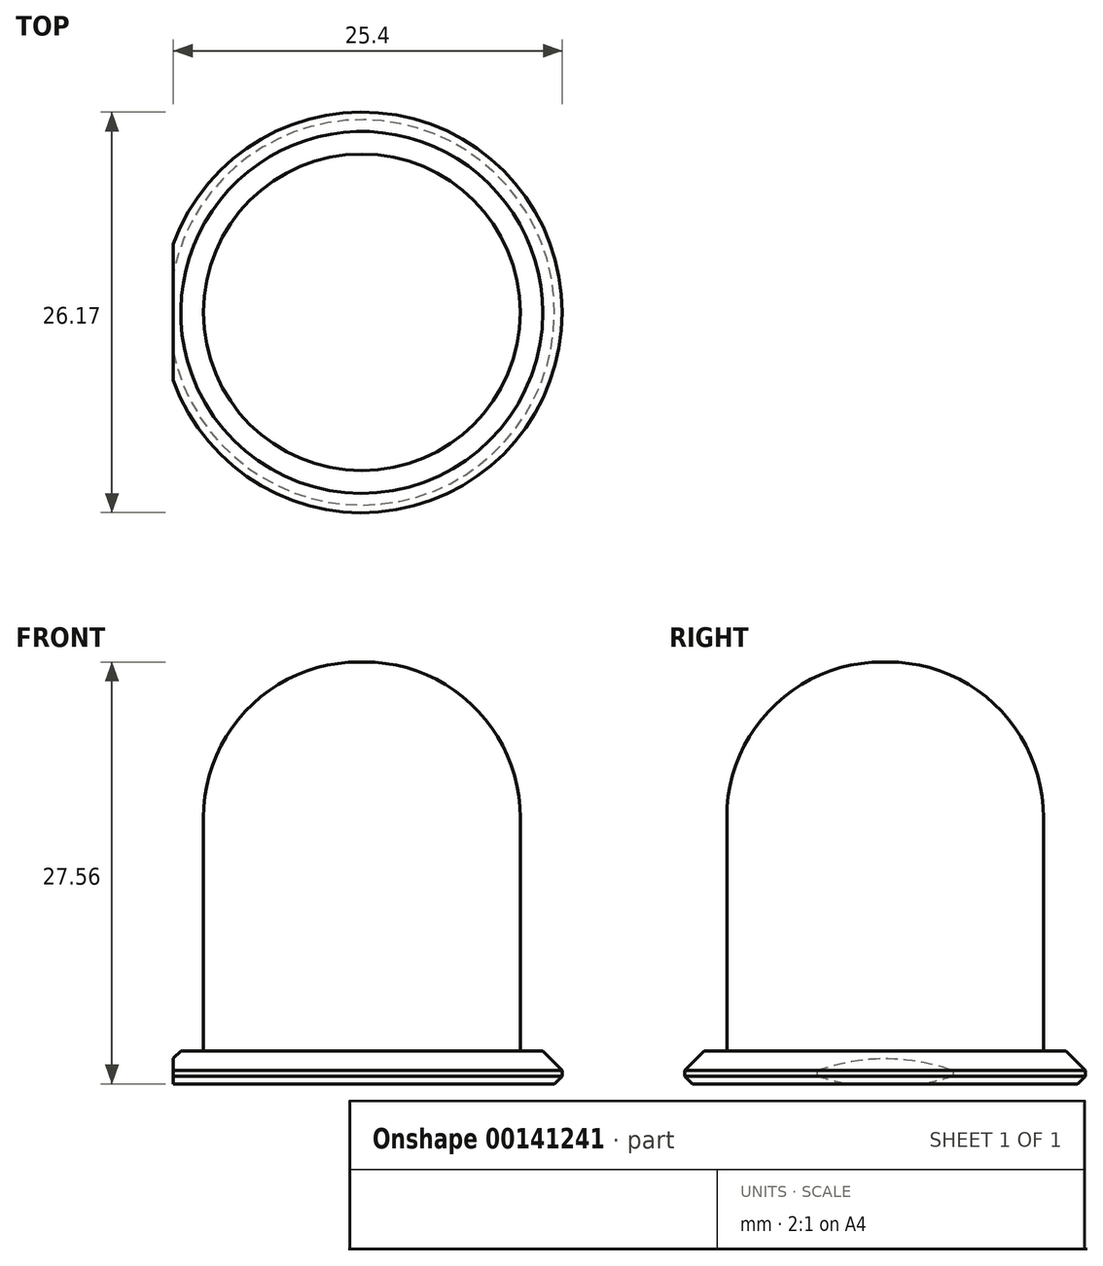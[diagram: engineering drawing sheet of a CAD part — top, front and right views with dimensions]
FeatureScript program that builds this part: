
annotation { "Feature Type Name" : "Feature", "Feature Type Description" : "" }
export const myFeature = defineFeature(function(context is Context, id is Id, definition is map)
    precondition{}
    {
        {
            var Q0;
            Q0=qCreatedBy(makeId("Top.planeOp"),FACE);
            var sketch = newSketch(context, id + "F0", { "sketchPlane" : qUnion([Q0])});
            skLineSegment(sketch, "E0", {"start": v(-68, 8.9) * mm, "end": v(-68, 0) * mm});
            skArc(sketch, "E1", {"start": v(-68, 0) * mm, "mid": v(-42.6, 4.44) * mm, "end": v(-68, 8.9) * mm});
            skSolve(sketch);
        }
        {
            var Q0;
            Q0=makeQuery(id+"F0.imprint","IMPRINT",FACE,{"disambiguationData":[TD([[makeQuery(id+"F0.imprint","IMPRINT",EDGE,{"derivedFrom":sQuery(id+"F0.wireOp",EDGE,"E0")}),1.0]])]});
            extrude(context, id + "F1", {"entities" : qUnion([Q0]), "depth" : 2.16 * mm});
        }
        {
            var Q0;
            Q0=makeQuery(id+"F1.opExtrude","CAP_FACE",FACE,{"disambiguationData":[OSD([sQuery(id+"F0.wireOp",EDGE,"E0"),sQuery(id+"F0.wireOp",EDGE,"E1")])],"isStart":false});
            var sketch = newSketch(context, id + "F2", { "sketchPlane" : qUnion([Q0])});
            skCircle(sketch, "E2", {"center": v(-55.7, 4.45) * mm, "radius": 10.34 * mm});
            skSolve(sketch);
        }
        {
            var Q0;
            Q0 = qSketchRegion(id + "F2", true);
            extrude(context, id + "F3", {"entities" : qUnion([Q0]), "operationType" : NewBodyOperationType.ADD, "depth" : 25.4 * mm});
        }
        {
            var Q0;
            Q0=makeQuery(id+"F1.opExtrude","CAP_EDGE",EDGE,{"disambiguationData":[OSD([sQuery(id+"F0.wireOp",EDGE,"E1")])],"isStart":false});
            chamfer(context, id + "F4", {"entities" : qUnion([Q0]), "width" : 1.27 * mm, "tangentPropagation" : true});
        }
        {
            var Q0;
            Q0=makeQuery(id+"F1.opExtrude","CAP_EDGE",EDGE,{"disambiguationData":[OSD([sQuery(id+"F0.wireOp",EDGE,"E1")])],"isStart":true});
            chamfer(context, id + "F5", {"entities" : qUnion([Q0]), "width" : 0.5 * mm, "tangentPropagation" : true});
        }
        {
            var Q0;
            Q0=makeQuery(id+"F3.opExtrude","CAP_FACE",FACE,{"disambiguationData":[OSD([sQuery(id+"F2.wireOp",EDGE,"E2")])],"isStart":false});
            fillet(context, id + "F6", {"entities" : qUnion([Q0]), "radius" : 10.16 * mm, "tangentPropagation" : true, "allowEdgeOverflow" : false});
        }
    });
